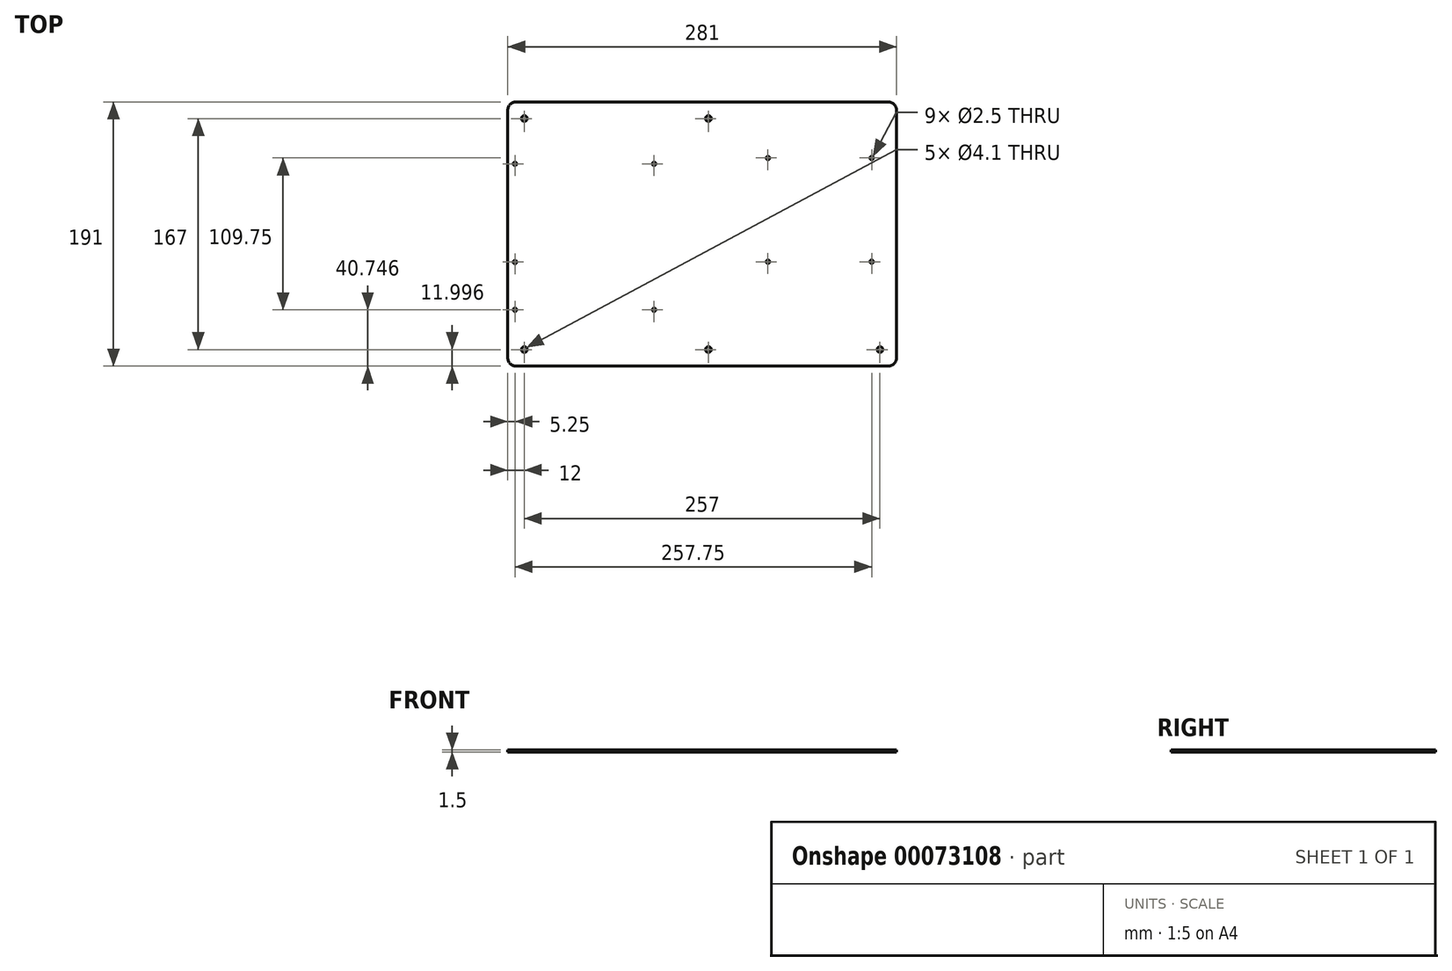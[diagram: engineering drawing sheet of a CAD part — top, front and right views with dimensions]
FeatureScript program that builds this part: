
annotation { "Feature Type Name" : "Feature", "Feature Type Description" : "" }
export const myFeature = defineFeature(function(context is Context, id is Id, definition is map)
    precondition{}
    {
        {
            var Q0;
            Q0=qCreatedBy(makeId("Top.planeOp"),FACE);
            var sketch = newSketch(context, id + "F0", { "sketchPlane" : qUnion([Q0])});
            skLineSegment(sketch, "E0.rect.bottom", {"start": v(-130, 98) * mm, "end": v(151, 98) * mm});
            skLineSegment(sketch, "E0.rect.top", {"start": v(-130, -93) * mm, "end": v(151, -93) * mm});
            skLineSegment(sketch, "E0.rect.left", {"start": v(-130, 98) * mm, "end": v(-130, -93) * mm});
            skLineSegment(sketch, "E0.rect.right", {"start": v(151, 98) * mm, "end": v(151, -93) * mm});
            skPoint(sketch, "E1", {"position": v(-124.75, -52.24) * mm});
            skPoint(sketch, "E2", {"position": v(-124.75, -17.75) * mm});
            skPoint(sketch, "E3", {"position": v(-124.75, 53.26) * mm});
            skPoint(sketch, "E4", {"position": v(-24.25, 53.26) * mm});
            skCircle(sketch, "E5", {"center": v(-124.75, 53.26) * mm, "radius": 1.25 * mm});
            skCircle(sketch, "E6", {"center": v(-24.25, 53.26) * mm, "radius": 1.25 * mm});
            skCircle(sketch, "E7", {"center": v(-124.75, -17.75) * mm, "radius": 1.25 * mm});
            skCircle(sketch, "E8", {"center": v(-124.75, -52.24) * mm, "radius": 1.25 * mm});
            skPoint(sketch, "E9", {"position": v(-22, 55.5) * mm});
            skPoint(sketch, "E10", {"position": v(-127, -54.5) * mm});
            skLineSegment(sketch, "E11.bottom", {"start": v(-22, 55.5) * mm, "end": v(-127, 55.5) * mm});
            skLineSegment(sketch, "E11.top", {"start": v(-22, -54.5) * mm, "end": v(-127, -54.5) * mm});
            skLineSegment(sketch, "E11.left", {"start": v(-22, 55.5) * mm, "end": v(-22, -54.5) * mm});
            skLineSegment(sketch, "E11.right", {"start": v(-127, 55.5) * mm, "end": v(-127, -54.5) * mm});
            skPoint(sketch, "E12", {"position": v(148, 95) * mm});
            skLineSegment(sketch, "E13.bottom", {"start": v(148, 95) * mm, "end": v(43, 95) * mm});
            skLineSegment(sketch, "E13.top", {"start": v(148, -55) * mm, "end": v(43, -55) * mm});
            skLineSegment(sketch, "E13.left", {"start": v(148, 95) * mm, "end": v(148, -55) * mm});
            skLineSegment(sketch, "E13.right", {"start": v(43, 95) * mm, "end": v(43, -55) * mm});
            skPoint(sketch, "E14", {"position": v(133, 57.5) * mm});
            skPoint(sketch, "E15", {"position": v(58, 57.5) * mm});
            skPoint(sketch, "E16", {"position": v(58, -17.5) * mm});
            skPoint(sketch, "E17", {"position": v(133, -17.5) * mm});
            skCircle(sketch, "E18", {"center": v(-24.25, -52.24) * mm, "radius": 1.25 * mm});
            skPoint(sketch, "E19", {"position": v(-118, 86) * mm});
            skPoint(sketch, "E20", {"position": v(15, 86) * mm});
            skPoint(sketch, "E21", {"position": v(139, -81) * mm});
            skPoint(sketch, "E22", {"position": v(-118, -81) * mm});
            skPoint(sketch, "E23", {"position": v(15, -81) * mm});
            skSolve(sketch);
        }
        {
            var Q0;
            Q0=makeQuery(id+"F0.imprint","IMPRINT",FACE,{"disambiguationData":[TD([[makeQuery(id+"F0.imprint","IMPRINT",EDGE,{"derivedFrom":sQuery(id+"F0.wireOp",EDGE,"E0.rect.bottom")}),-1.0]])]});
            var Q1;
            Q1=makeQuery(id+"F0.imprint","IMPRINT",FACE,{"disambiguationData":[TD([[makeQuery(id+"F0.imprint","IMPRINT",EDGE,{"derivedFrom":sQuery(id+"F0.wireOp",EDGE,"E5")}),-1.0]])]});
            var Q2;
            Q2=makeQuery(id+"F0.imprint","IMPRINT",FACE,{"disambiguationData":[TD([[makeQuery(id+"F0.imprint","IMPRINT",EDGE,{"derivedFrom":sQuery(id+"F0.wireOp",EDGE,"E13.bottom")}),1.0]])]});
            var Q3;
            Q3=makeQuery(id+"F0.imprint","IMPRINT",FACE,{"disambiguationData":[TD([[makeQuery(id+"F0.imprint","IMPRINT",EDGE,{"derivedFrom":sQuery(id+"F0.wireOp",EDGE,"E6")}),1.0]])]});
            var Q4;
            Q4=makeQuery(id+"F0.imprint","IMPRINT",FACE,{"disambiguationData":[TD([[makeQuery(id+"F0.imprint","IMPRINT",EDGE,{"derivedFrom":sQuery(id+"F0.wireOp",EDGE,"E5")}),1.0]])]});
            var Q5;
            Q5=makeQuery(id+"F0.imprint","IMPRINT",FACE,{"disambiguationData":[TD([[makeQuery(id+"F0.imprint","IMPRINT",EDGE,{"derivedFrom":sQuery(id+"F0.wireOp",EDGE,"E8")}),1.0]])]});
            var Q6;
            Q6=makeQuery(id+"F0.imprint","IMPRINT",FACE,{"disambiguationData":[TD([[makeQuery(id+"F0.imprint","IMPRINT",EDGE,{"derivedFrom":sQuery(id+"F0.wireOp",EDGE,"E18")}),1.0]])]});
            var Q7;
            Q7=makeQuery(id+"F0.imprint","IMPRINT",FACE,{"disambiguationData":[TD([[makeQuery(id+"F0.imprint","IMPRINT",EDGE,{"derivedFrom":sQuery(id+"F0.wireOp",EDGE,"E7")}),1.0]])]});
            extrude(context, id + "F1", {"entities" : qUnion([Q0, Q1, Q2, Q3, Q4, Q5, Q6, Q7]), "depth" : 1.5 * mm});
        }
        {
            var Q0;
            Q0=makeQuery(id+"F0.imprint","IMPRINT",FACE,{"disambiguationData":[TD([[makeQuery(id+"F0.imprint","IMPRINT",EDGE,{"derivedFrom":sQuery(id+"F0.wireOp",EDGE,"E5")}),1.0]])]});
            var Q1;
            Q1=makeQuery(id+"F0.imprint","IMPRINT",FACE,{"disambiguationData":[TD([[makeQuery(id+"F0.imprint","IMPRINT",EDGE,{"derivedFrom":sQuery(id+"F0.wireOp",EDGE,"E6")}),1.0]])]});
            var Q2;
            Q2=makeQuery(id+"F0.imprint","IMPRINT",FACE,{"disambiguationData":[TD([[makeQuery(id+"F0.imprint","IMPRINT",EDGE,{"derivedFrom":sQuery(id+"F0.wireOp",EDGE,"E18")}),1.0]])]});
            var Q3;
            Q3=makeQuery(id+"F0.imprint","IMPRINT",FACE,{"disambiguationData":[TD([[makeQuery(id+"F0.imprint","IMPRINT",EDGE,{"derivedFrom":sQuery(id+"F0.wireOp",EDGE,"E8")}),1.0]])]});
            extrude(context, id + "F2", {"entities" : qUnion([Q0, Q1, Q2, Q3]), "operationType" : NewBodyOperationType.REMOVE, "depth" : 25 * mm});
        }
        {
            var Q0;
            Q0=sQuery(id+"F0.wireOp",VERTEX,"E14");
            var Q1;
            Q1=sQuery(id+"F0.wireOp",VERTEX,"E15");
            var Q2;
            Q2=sQuery(id+"F0.wireOp",VERTEX,"E16");
            var Q3;
            Q3=sQuery(id+"F0.wireOp",VERTEX,"E17");
            var Q4;
            Q4=sQuery(id+"F0.wireOp",VERTEX,"E2");
            var Q5;
            Q5=makeQuery(id+"F1.opExtrude","SWEPT_BODY",BODY,{"disambiguationData":[OSD([sQuery(id+"F0.wireOp",EDGE,"E0.rect.bottom"),sQuery(id+"F0.wireOp",EDGE,"E0.rect.top"),sQuery(id+"F0.wireOp",EDGE,"E0.rect.left"),sQuery(id+"F0.wireOp",EDGE,"E0.rect.right")])]});
            hole(context, id + "F3", {"style" : HoleStyle.SIMPLE, "holeDiameter" : 2.5 * mm, "endStyle" : HoleEndStyle.THROUGH, "oppositeDirection" : true, "locations" : qUnion([Q0, Q1, Q2, Q3, Q4]), "scope" : qUnion([Q5]), "isTappedThrough" : true});
        }
        {
            var Q0;
            Q0=sQuery(id+"F0.wireOp",VERTEX,"E19");
            var Q1;
            Q1=sQuery(id+"F0.wireOp",VERTEX,"E20");
            var Q2;
            Q2=sQuery(id+"F0.wireOp",VERTEX,"E21");
            var Q3;
            Q3=sQuery(id+"F0.wireOp",VERTEX,"E22");
            var Q4;
            Q4=sQuery(id+"F0.wireOp",VERTEX,"E23");
            var Q5;
            Q5=makeQuery(id+"F1.opExtrude","SWEPT_BODY",BODY,{"disambiguationData":[OSD([sQuery(id+"F0.wireOp",EDGE,"E0.rect.bottom"),sQuery(id+"F0.wireOp",EDGE,"E0.rect.top"),sQuery(id+"F0.wireOp",EDGE,"E0.rect.left"),sQuery(id+"F0.wireOp",EDGE,"E0.rect.right")])]});
            hole(context, id + "F4", {"style" : HoleStyle.SIMPLE, "endStyle" : HoleEndStyle.THROUGH, "oppositeDirection" : true, "standardTappedOrClearance" : lookupTablePath({ "standard" : "ISO", "size" : "4.1", "type" : "Drilled" }), "standardBlindInLast" : lookupTablePath({ "standard" : "ISO", "size" : "4.1", "type" : "Drilled" }), "holeDiameter" : 4.1 * mm, "locations" : qUnion([Q0, Q1, Q2, Q3, Q4]), "scope" : qUnion([Q5]), "isTappedThrough" : true});
        }
        {
            var Q0;
            Q0=makeQuery(id+"F1.opExtrude","SWEPT_EDGE",EDGE,{"disambiguationData":[OSD([sQuery(id+"F0.wireOp",EDGE,"E0.rect.bottom"),sQuery(id+"F0.wireOp",EDGE,"E0.rect.left")])]});
            var Q1;
            Q1=makeQuery(id+"F1.opExtrude","SWEPT_EDGE",EDGE,{"disambiguationData":[OSD([sQuery(id+"F0.wireOp",EDGE,"E0.rect.top"),sQuery(id+"F0.wireOp",EDGE,"E0.rect.left")])]});
            var Q2;
            Q2=makeQuery(id+"F1.opExtrude","SWEPT_EDGE",EDGE,{"disambiguationData":[OSD([sQuery(id+"F0.wireOp",EDGE,"E0.rect.top"),sQuery(id+"F0.wireOp",EDGE,"E0.rect.right")])]});
            var Q3;
            Q3=makeQuery(id+"F1.opExtrude","SWEPT_EDGE",EDGE,{"disambiguationData":[OSD([sQuery(id+"F0.wireOp",EDGE,"E0.rect.bottom"),sQuery(id+"F0.wireOp",EDGE,"E0.rect.right")])]});
            fillet(context, id + "F5", {"entities" : qUnion([Q0, Q1, Q2, Q3]), "radius" : 6 * mm, "tangentPropagation" : true, "allowEdgeOverflow" : false});
        }
        {
            var Q0;
            Q0=makeQuery(id+"F1.opExtrude","SWEPT_BODY",BODY,{"disambiguationData":[OSD([sQuery(id+"F0.wireOp",EDGE,"E0.rect.bottom"),sQuery(id+"F0.wireOp",EDGE,"E0.rect.top"),sQuery(id+"F0.wireOp",EDGE,"E0.rect.left"),sQuery(id+"F0.wireOp",EDGE,"E0.rect.right")])]});
            var Q1;
            {var subQ0=sQuery(id+"F0.wireOp",EDGE,"E0.rect.top");Q1=makeQuery(id+"F5.opFillet","BLEND_EDGE",EDGE,{"blendedFrom":[makeQuery(id+"F1.opExtrude","SWEPT_EDGE",EDGE,{"disambiguationData":[OSD([subQ0,sQuery(id+"F0.wireOp",EDGE,"E0.rect.right")])]}),makeQuery(id+"F1.opExtrude","SWEPT_FACE",FACE,{"disambiguationData":[OSD([subQ0])]})],"blendedInto":[makeQuery(id+"F1.opExtrude","SWEPT_FACE",FACE,{"disambiguationData":[OSD([subQ0])]})]});}
            transform(context, id + "F6", {"entities" : qUnion([Q0]), "transformType" : TransformType.TRANSLATION_3D, "dx" : 0 * mm, "dy" : 0 * mm, "dz" : 10 * mm, "makeCopy" : false});
        }
        {
            var Q0;
            Q0=makeQuery(id+"F1.opExtrude","SWEPT_BODY",BODY,{"disambiguationData":[OSD([sQuery(id+"F0.wireOp",EDGE,"E0.rect.bottom"),sQuery(id+"F0.wireOp",EDGE,"E0.rect.top"),sQuery(id+"F0.wireOp",EDGE,"E0.rect.left"),sQuery(id+"F0.wireOp",EDGE,"E0.rect.right")])]});
            transform(context, id + "F7", {"entities" : qUnion([Q0]), "transformType" : TransformType.TRANSLATION_3D, "dx" : 2 * mm, "dy" : 0 * mm, "dz" : 0 * mm, "makeCopy" : false});
        }
    });
